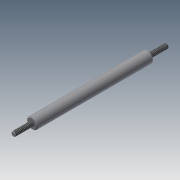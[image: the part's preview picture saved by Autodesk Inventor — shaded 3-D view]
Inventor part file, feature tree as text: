
AUTODESK INVENTOR PART (.ipt)
format: ipt  version: 2015 (Build 190159000, 159)  size: 113,152 bytes
history: native  units: mm
features: sketch x6, extrude x3, chamfer x3, hole x2, thread x2
ambient origin geometry x8: Origin, YZ Plane, XZ Plane, XY Plane, X Axis, Y Axis, Z Axis, Center Point
bodies: Solid1 (feature_tree)
feature tree (16):
  extrude  "Extrusion1"  Depth=62.7mm TaperAngle=0.0deg
  hole  "Hole1"  [1 undecoded]
  hole  "Hole2"  [1 undecoded]
  chamfer  "Chamfer1"  Distance=10.0mm
  extrude  "Extrusion2"  Depth=10.0mm TaperAngle=0.0deg
  extrude  "Extrusion3"  [1 undecoded]
  sketch  "Sketch6"  dims[d31=0.3mm d32=2.0mm d33=45.0deg]
  thread  "Thread1"  [1 undecoded]
  chamfer  "Chamfer2"  [1 undecoded]
  thread  "Thread2"  [1 undecoded]
  chamfer  "Chamfer3"  [1 undecoded]
  sketch  "Sketch1"  dims[d0=6.0mm d1=62.7mm d2=0.0mm]
  sketch  "Sketch2"  dims[d3=2.459mm d4=6.0mm d5=4.0mm d6=2.0mm d7=90.0deg d8=8.0mm d9=0.0mm]
  sketch  "Sketch3"  dims[d10=2.459mm d11=6.0mm d12=4.0mm d13=2.0mm d14=90.0deg d15=8.0mm d16=0.0mm d17=0.5mm d18=2.0mm d19=45.0deg]
  sketch  "Sketch4"  dims[d20=10.0mm d21=0.0mm d22=10.0mm d23=0.0mm d24=10.0mm d25=0.0mm]
  sketch  "Sketch5"  dims[d26=0.3mm d27=2.0mm d28=45.0deg d29=10.0mm d30=0.0mm]
note: 7 required parameter values undecoded (feature->parameter linkage not recoverable at this tier; creation-order binding heuristic only, values carry confidence <= 0.55)
